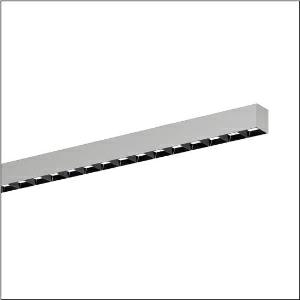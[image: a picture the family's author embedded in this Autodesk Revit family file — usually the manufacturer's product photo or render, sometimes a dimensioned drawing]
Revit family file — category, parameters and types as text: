
# Revit family: silica_r__21_51mx24dc3asb_5aec
name_source: partatom
category: Lighting Fixtures
units: mm (PartAtom-declared; Revit-internal decimal feet)

## family parameters
Cut with Voids When Loaded = No
Host = Face
Light Source = No
Part Type = Normal
Room Calculation Point = No
Round Connector Dimension = Use Diameter
Shared = No

## types (1)
- --- (1 x LED, 10800 lm, 79 W, 3000K)
    Apparent Load = 79 VA
    CIE Flux Codes = 74 94 99 100 100
    Color Rendering = 80
    Color Temperature = 3000K
    Default Elevation = 1800 mm
    Description = Silica® 21, office luminaire, primary light control with darklight reflector, of PMMA, black, CAT 2 (L<= 3000cd/m²), light emission: direct distribution, primary light characteristic: asymmetric, installation type: surface-mounted, LED, rated luminous flux: 10.800lm, luminous efficacy: 137lm/W, light colour: 830, colour temperature: 3000K, with terminal, 3+2-pole, max. 2.5mm², mains connection: 220..240V, AC, 50/60Hz, rated input power: 79W, luminaire housing, of aluminium, metallic grey (RAL 9006), length: 3.004mm, width: 53mm, height: 53mm, protection rating (complete): IP20, insulation class (complete): insulation class I (protective earthing), certification: CE, permissible operating ambient temperature: 0..+35°C, standard: EN 50419, packaging unit: 1 piece
    Height = 0 mm  [stored 0 ft]
    Lamp = 1 x LED
    Lamp Light Flux = 10800 lm
    Lamp Power = 79 W
    Lamp count = 1
    Length = 3004 mm
    Luminous efficacy = 137 lm/W
    Manufacturer = Siteco
    ModVariant = No
    Model = 51MX24DC3ASB
    Mounting Place = Ceiling
    Mounting Type = Recessed
    Number of Poles = 1
    OnlyDefault = Yes
    Power Factor = 1
    Product Name = Silica® 21
    Product group = office luminaire | ceiling recessed
    ProductGroupID = 401
    Protection Class = Protection class I
    Protection Degree = IP 20
    RLX_Detail_Level = 1
    RLX_Emergency_Light_Flux = 0 lm
    RLX_Emergency_Type = 0
    RLX_Emergency_Type_DB = No
    RlxData = <blob elided: 63985 chars, md5=04993e55>
    Socket = socket
    Standby Power = 0 W
    System Light Flux = 10800 lm
    System Power = 79 W
    Type Comments = factory setting: luminous flux: 100 % | dim-lin: 254 | 448 mA
    Type Image = l_1297764.jpg
    URL = http://relux.com
    VarID = @adj_053267
    Voltage = 0 V
    Weight = 0.00 kg
    Width = 53 mm

note: [stored X ft] marks values corroborated as IEEE doubles in the binary element streams (Revit-internal decimal feet)

## geometry (parser evidence)
native form markers: Blend x4, Sweep x11
no freeform markers — native parametric forms only
